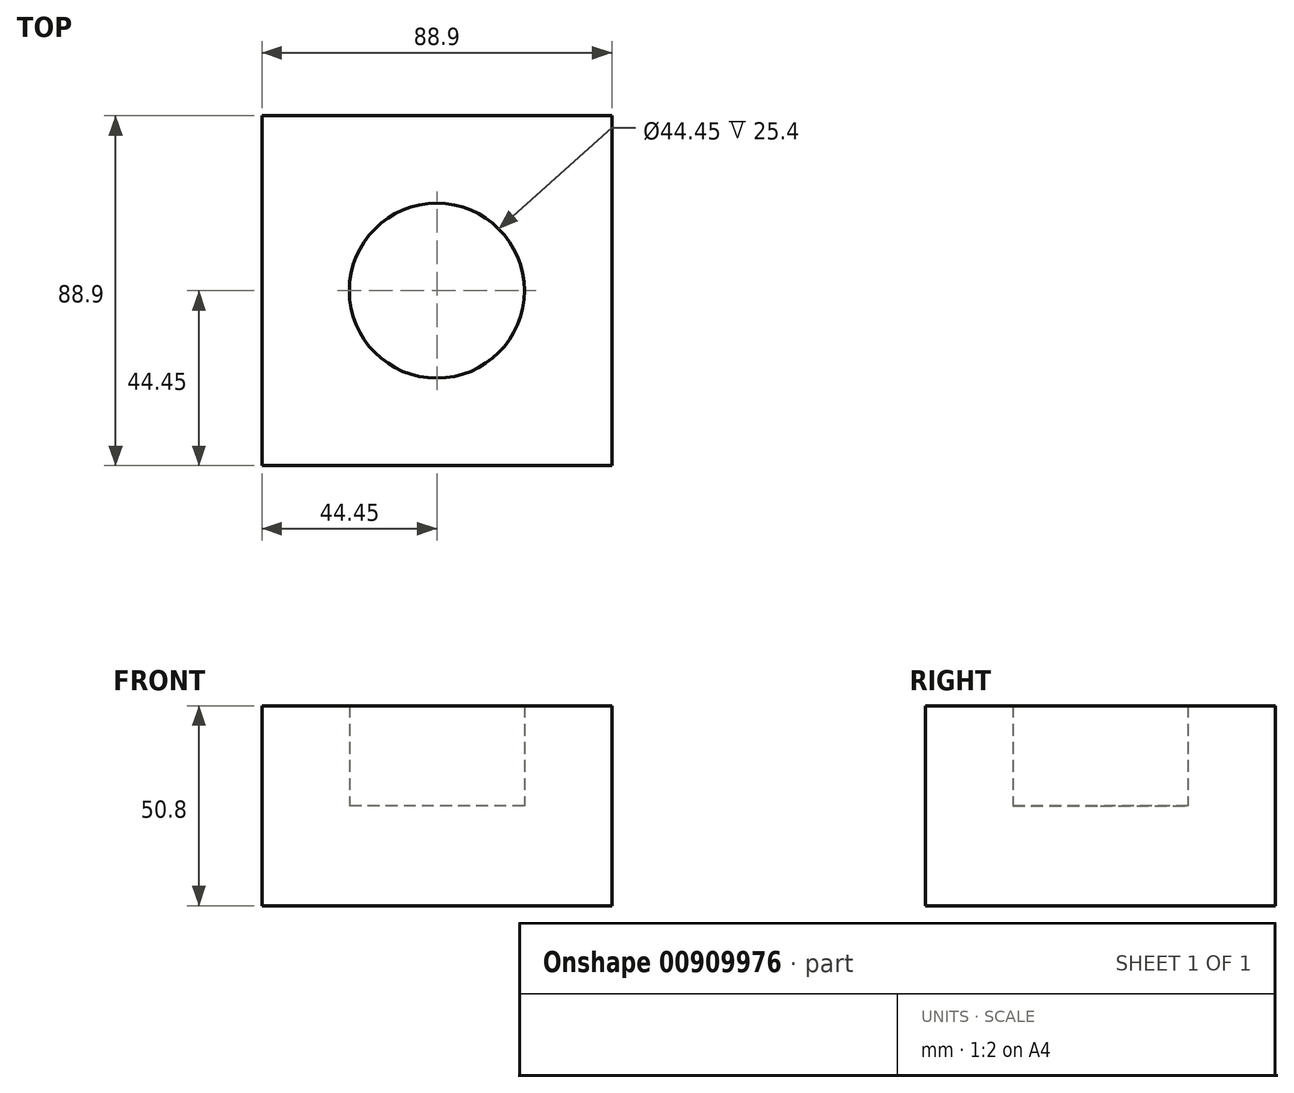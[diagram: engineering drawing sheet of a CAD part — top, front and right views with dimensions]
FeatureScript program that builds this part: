
annotation { "Feature Type Name" : "Feature", "Feature Type Description" : "" }
export const myFeature = defineFeature(function(context is Context, id is Id, definition is map)
    precondition{}
    {
        {
            var Q0;
            Q0=qCreatedBy(makeId("Top.planeOp"),FACE);
            var sketch = newSketch(context, id + "F0", { "sketchPlane" : qUnion([Q0])});
            skCircle(sketch, "E0", {"center": v(0, 0) * mm, "radius": 22.23 * mm});
            skLineSegment(sketch, "E1.bottom", {"start": v(-44.45, 44.45) * mm, "end": v(44.45, 44.45) * mm});
            skLineSegment(sketch, "E1.top", {"start": v(-44.45, -44.45) * mm, "end": v(44.45, -44.45) * mm});
            skLineSegment(sketch, "E1.left", {"start": v(-44.45, 44.45) * mm, "end": v(-44.45, -44.45) * mm});
            skLineSegment(sketch, "E1.right", {"start": v(44.45, 44.45) * mm, "end": v(44.45, -44.45) * mm});
            skLineSegment(sketch, "E2", {"start": v(-44.45, 44.45) * mm, "end": v(44.45, -44.45) * mm, "construction": true});
            skLineSegment(sketch, "E3", {"start": v(44.45, 44.45) * mm, "end": v(-44.45, -44.45) * mm, "construction": true});
            skSolve(sketch);
        }
        {
            var Q0;
            Q0=makeQuery(id+"F0.imprint","IMPRINT",FACE,{"disambiguationData":[TD([[makeQuery(id+"F0.imprint","IMPRINT",EDGE,{"derivedFrom":sQuery(id+"F0.wireOp",EDGE,"E0")}),-1.0]])]});
            extrude(context, id + "F1", {"entities" : qUnion([Q0]), "depth" : 50.8 * mm, "offsetDistance" : 25 * mm});
        }
        {
            var Q0;
            Q0=makeQuery(id+"F0.imprint","IMPRINT",FACE,{"disambiguationData":[TD([[makeQuery(id+"F0.imprint","IMPRINT",EDGE,{"derivedFrom":sQuery(id+"F0.wireOp",EDGE,"E0")}),1.0]])]});
            extrude(context, id + "F2", {"entities" : qUnion([Q0]), "operationType" : NewBodyOperationType.ADD, "depth" : 25.4 * mm, "offsetDistance" : 25 * mm});
        }
    });
